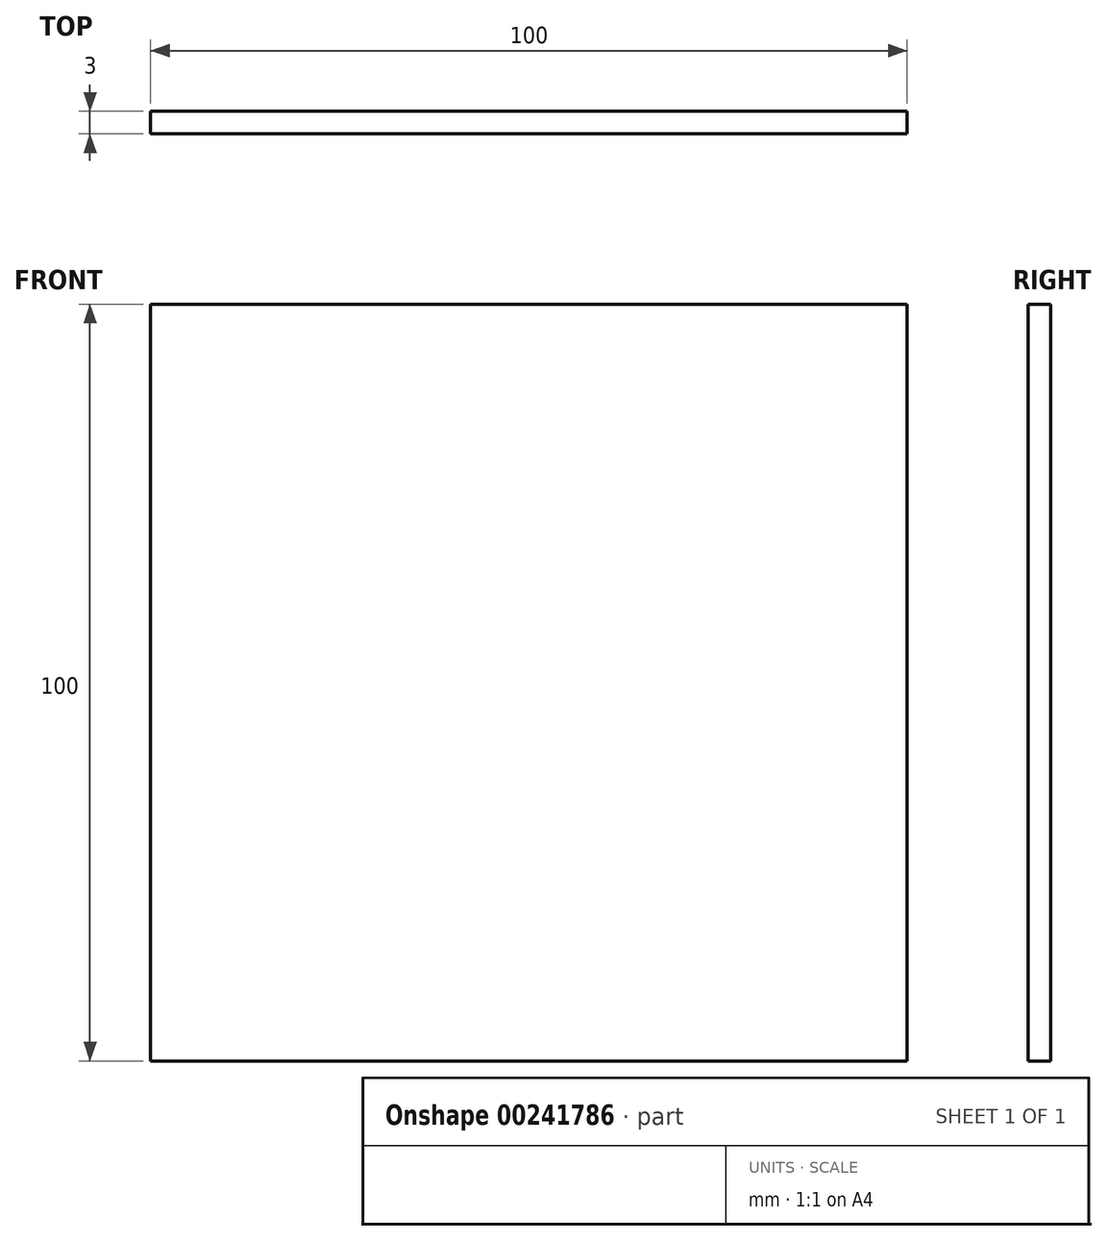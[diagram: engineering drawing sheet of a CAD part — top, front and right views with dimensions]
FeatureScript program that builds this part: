
annotation { "Feature Type Name" : "Feature", "Feature Type Description" : "" }
export const myFeature = defineFeature(function(context is Context, id is Id, definition is map)
    precondition{}
    {
        {
            var Q0;
            Q0=qCreatedBy(makeId("Front.planeOp"),FACE);
            var sketch = newSketch(context, id + "F0", { "sketchPlane" : qUnion([Q0])});
            skLineSegment(sketch, "E0.bottom", {"start": v(0, 0) * mm, "end": v(100, 0) * mm});
            skLineSegment(sketch, "E0.top", {"start": v(0, 100) * mm, "end": v(100, 100) * mm});
            skLineSegment(sketch, "E0.left", {"start": v(0, 0) * mm, "end": v(0, 100) * mm});
            skLineSegment(sketch, "E0.right", {"start": v(100, 0) * mm, "end": v(100, 100) * mm});
            skSolve(sketch);
        }
        {
            var Q0;
            Q0=qSketchRegion(id+"F0",true);
            extrude(context, id + "F1", {"entities" : qUnion([Q0]), "depth" : 3 * mm});
        }
    });
